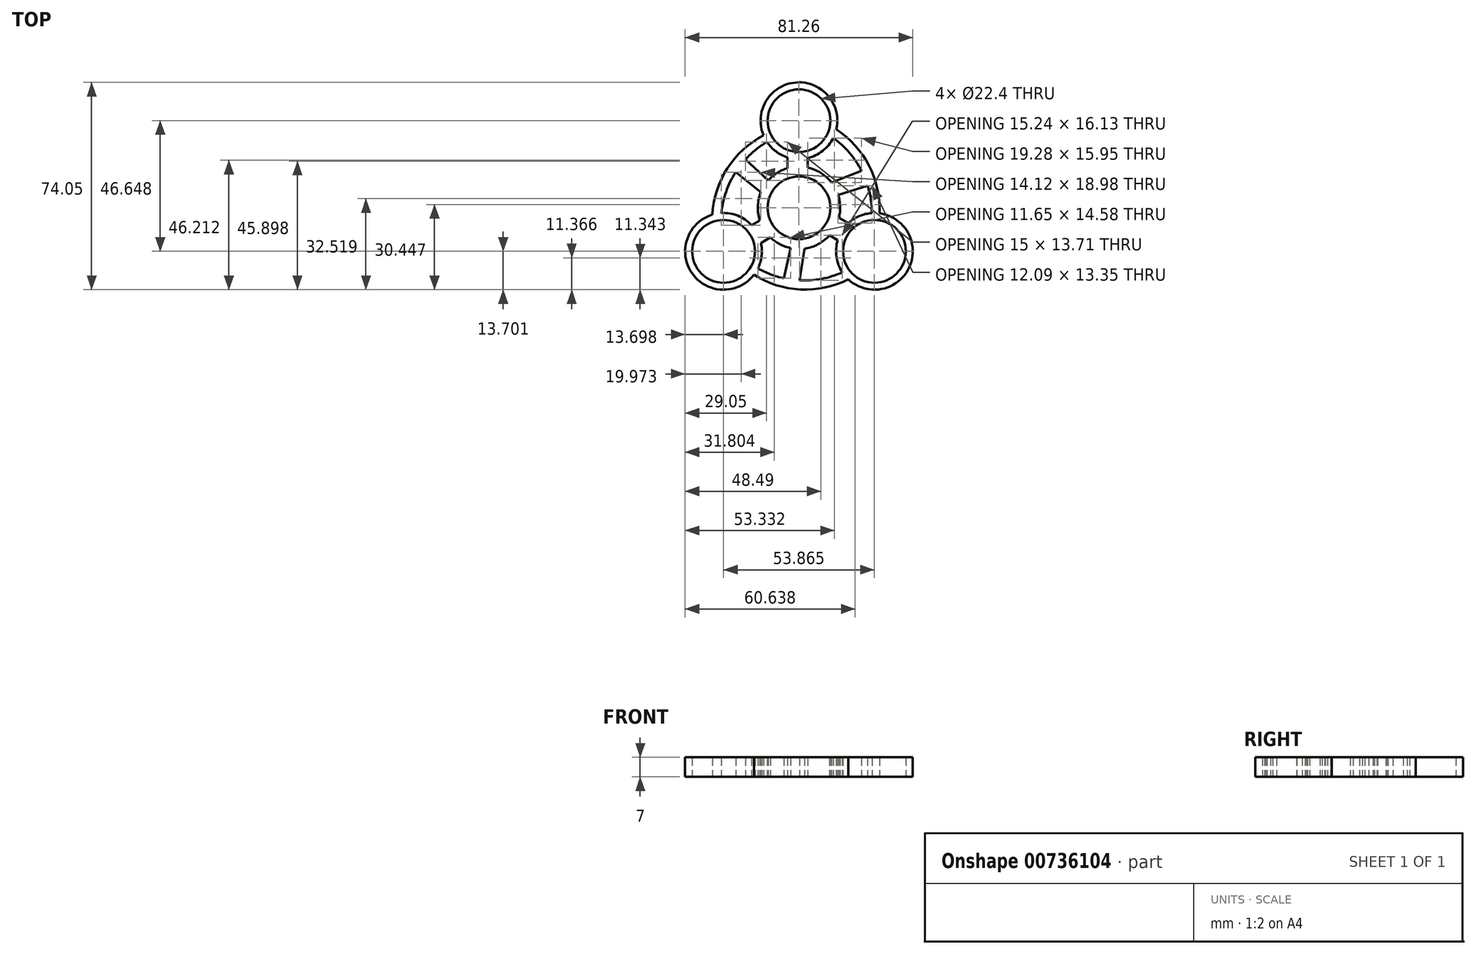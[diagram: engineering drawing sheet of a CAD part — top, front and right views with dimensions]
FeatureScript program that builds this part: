
annotation { "Feature Type Name" : "Feature", "Feature Type Description" : "" }
export const myFeature = defineFeature(function(context is Context, id is Id, definition is map)
    precondition{}
    {
        {
            var Q0;
            Q0=qCreatedBy(makeId("Top.planeOp"),FACE);
            var sketch = newSketch(context, id + "F0", { "sketchPlane" : qUnion([Q0])});
            skCircle(sketch, "E0", {"center": v(0, 0) * mm, "radius": 11.2 * mm});
            skCircle(sketch, "E1", {"center": v(0, 31.1) * mm, "radius": 11.2 * mm});
            skArc(sketch, "E2", {"start": v(13.35, 28) * mm, "mid": v(-1.12, 44.75) * mm, "end": v(-12.66, 25.87) * mm});
            skArc(sketch, "E3", {"start": v(11.63, 8.99) * mm, "mid": v(7.83, 12.44) * mm, "end": v(3.06, 14.38) * mm});
            skCircle(sketch, "E4.1.0", {"center": v(-26.93, -15.55) * mm, "radius": 11.2 * mm});
            skArc(sketch, "E4.1.1", {"start": v(-14.65, -21.62) * mm, "mid": v(-15.5, -8) * mm, "end": v(-27.72, -1.87) * mm});
            skCircle(sketch, "E4.2.0", {"center": v(26.93, -15.55) * mm, "radius": 11.2 * mm});
            skArc(sketch, "E4.2.1", {"start": v(17.58, -25.56) * mm, "mid": v(39.32, -21.4) * mm, "end": v(28.73, -1.97) * mm});
            skArc(sketch, "E5", {"start": v(26.05, -1.88) * mm, "mid": v(25.65, 3.05) * mm, "end": v(24.52, 7.87) * mm});
            skArc(sketch, "E6", {"start": v(28.73, -1.97) * mm, "mid": v(25, 15.05) * mm, "end": v(13.35, 28) * mm});
            skArc(sketch, "E7.1.0", {"start": v(-11.4, 23.5) * mm, "mid": v(-15.47, 20.69) * mm, "end": v(-19.08, 17.3) * mm});
            skArc(sketch, "E7.1.1", {"start": v(-12.66, 25.87) * mm, "mid": v(-25.53, 14.12) * mm, "end": v(-30.92, -2.44) * mm});
            skArc(sketch, "E7.2.0", {"start": v(-14.65, -21.62) * mm, "mid": v(-10.18, -23.74) * mm, "end": v(-5.45, -25.17) * mm});
            skArc(sketch, "E7.2.1", {"start": v(-16.07, -23.9) * mm, "mid": v(0.53, -29.17) * mm, "end": v(17.58, -25.56) * mm});
            skLineSegment(sketch, "E8", {"start": v(-19.08, 17.3) * mm, "end": v(-10.96, 9.8) * mm});
            skLineSegment(sketch, "E9", {"start": v(-10.96, 9.8) * mm, "end": v(-13.6, 5.58) * mm});
            skLineSegment(sketch, "E10", {"start": v(-13.6, 5.58) * mm, "end": v(-22.58, 12.76) * mm});
            skLineSegment(sketch, "E11.1.0", {"start": v(1.97, -14.57) * mm, "end": v(0.24, -25.94) * mm});
            skLineSegment(sketch, "E11.1.1", {"start": v(-5.45, -25.17) * mm, "end": v(-3, -14.4) * mm});
            skLineSegment(sketch, "E11.2.0", {"start": v(11.63, 8.99) * mm, "end": v(22.34, 13.18) * mm});
            skLineSegment(sketch, "E11.2.1", {"start": v(24.52, 7.87) * mm, "end": v(13.96, 4.6) * mm});
            skArc(sketch, "E12.trimOffspring", {"start": v(-22.58, 12.76) * mm, "mid": v(-26, 5.75) * mm, "end": v(-27.72, -1.87) * mm});
            skArc(sketch, "E13.trimOffspring", {"start": v(22.34, 13.18) * mm, "mid": v(17.98, 19.65) * mm, "end": v(12.24, 24.94) * mm});
            skArc(sketch, "E14.trimOffspring", {"start": v(0.24, -25.94) * mm, "mid": v(8.03, -25.4) * mm, "end": v(15.48, -23.07) * mm});
            skArc(sketch, "E15.trimOffspring", {"start": v(26.05, -1.88) * mm, "mid": v(14.67, -9.43) * mm, "end": v(15.48, -23.07) * mm});
            skArc(sketch, "E16.trimOffspring", {"start": v(-13.6, 5.58) * mm, "mid": v(-14.69, 0.56) * mm, "end": v(-13.98, -4.54) * mm});
            skArc(sketch, "E17.trimOffspring", {"start": v(1.97, -14.57) * mm, "mid": v(6.86, -13) * mm, "end": v(10.92, -9.84) * mm});
            skArc(sketch, "E18.trimOffspring", {"start": v(-30.92, -2.44) * mm, "mid": v(-38.2, -23.35) * mm, "end": v(-16.07, -23.9) * mm});
            skArc(sketch, "E19.trimOffspring", {"start": v(-11.4, 23.5) * mm, "mid": v(0.83, 17.42) * mm, "end": v(12.24, 24.94) * mm});
            skLineSegment(sketch, "E20", {"start": v(-4.08, 18.02) * mm, "end": v(-4.08, 14.12) * mm});
            skLineSegment(sketch, "E21", {"start": v(3.06, 17.75) * mm, "end": v(3.06, 14.38) * mm});
            skLineSegment(sketch, "E22.1.0", {"start": v(-13.57, -12.55) * mm, "end": v(-10.19, -10.6) * mm});
            skLineSegment(sketch, "E22.1.1", {"start": v(-16.9, -6.22) * mm, "end": v(-13.98, -4.54) * mm});
            skLineSegment(sketch, "E22.2.0", {"start": v(17.65, -5.48) * mm, "end": v(14.27, -3.53) * mm});
            skLineSegment(sketch, "E22.2.1", {"start": v(13.84, -11.52) * mm, "end": v(10.92, -9.84) * mm});
            skArc(sketch, "E23.trimOffspring", {"start": v(-4.08, 14.12) * mm, "mid": v(-7.83, 12.44) * mm, "end": v(-10.96, 9.8) * mm});
            skArc(sketch, "E24.trimOffspring", {"start": v(14.27, -3.53) * mm, "mid": v(14.69, 0.56) * mm, "end": v(13.96, 4.6) * mm});
            skArc(sketch, "E25.trimOffspring", {"start": v(-10.19, -10.6) * mm, "mid": v(-6.86, -13) * mm, "end": v(-3, -14.4) * mm});
            skSolve(sketch);
        }
        {
            var Q0;
            Q0=makeQuery(id+"F0.imprint","IMPRINT",FACE,{"disambiguationData":[TD([[makeQuery(id+"F0.imprint","IMPRINT",EDGE,{"derivedFrom":sQuery(id+"F0.wireOp",EDGE,"E0")}),-1.0]])]});
            extrude(context, id + "F1", {"entities" : qUnion([Q0]), "depth" : 7 * mm, "offsetDistance" : 25 * mm});
        }
    });
